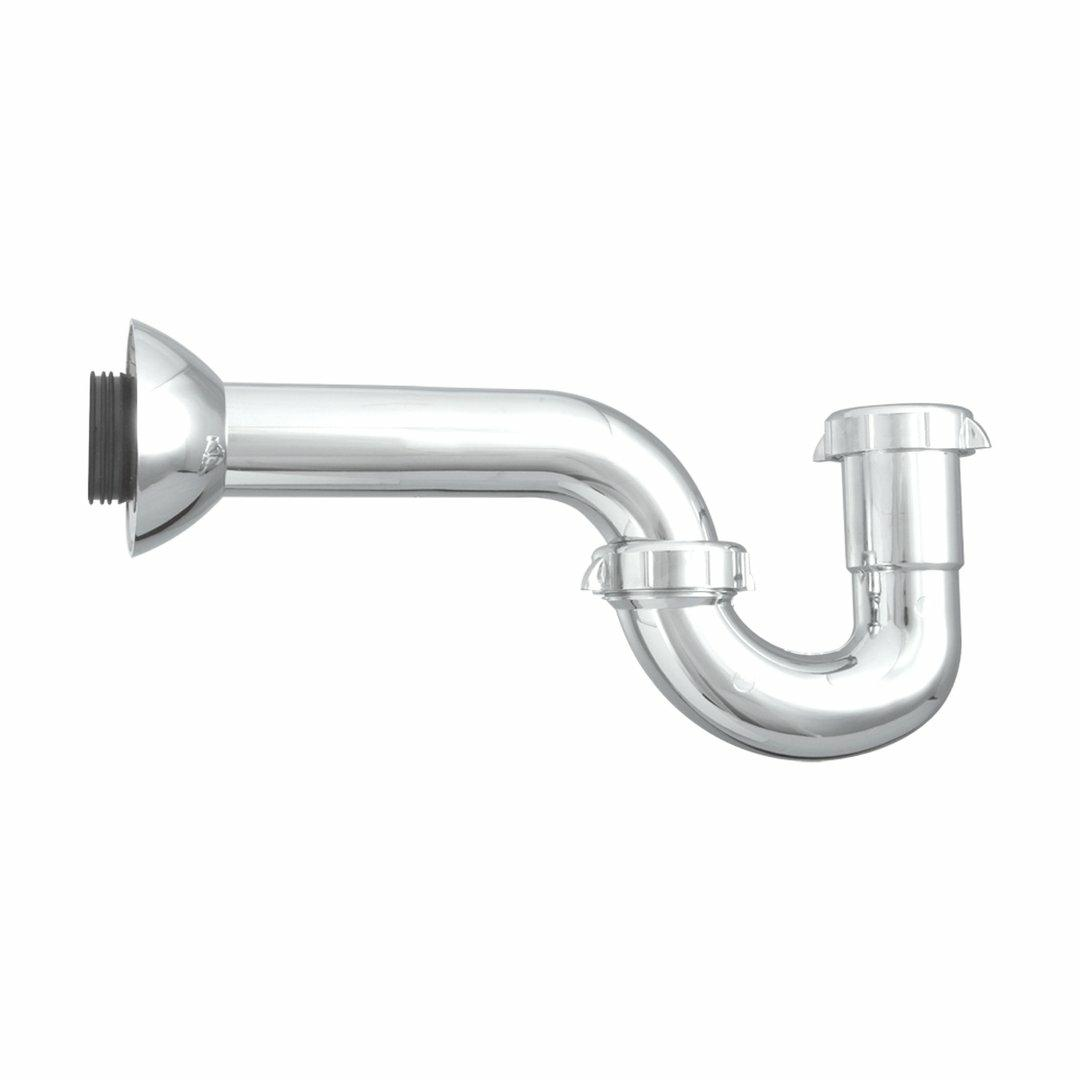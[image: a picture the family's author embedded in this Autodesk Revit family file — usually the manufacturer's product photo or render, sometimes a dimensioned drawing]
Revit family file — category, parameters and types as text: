
# Revit family: BIM_L1-3079-11
name_source: partatom
category: Aparatos sanitarios
units: mm (PartAtom-declared; Revit-internal decimal feet)

## family parameters
Activar corte en vistas = No
Anfitrión = Cara
Compartido = No
Corte con vacíos al cargar = No
Cota de conector redondo = Usar diámetro
Mantener orientación de anotación = No
Número OmniClass = 23.31.11.00
Punto de cálculo de habitación = No
Tipo de pieza = Normal

## types (1)
- L1-3079-11
    Acabado = Cepillado Brillante
    Alto = 190 mm
    Ancho = 1200 mm  [stored 3.93701 ft]
    Conexión AC = Sí
    Conexión AF = Sí
    Conexión de residuos = No
    Conexión de ventilación = No
    Date Modified = 08-08-2025
    Descripción = Lavaplatos en acero
    Elevación por defecto = 0 mm  [stored 0 ft]
    Fabricante = Gricol
    Garantia Especifica = 5 años
    Imagen de tipo = <Ninguno>
    Largo = 510 mm  [stored 1.67323 ft]
    Link Ficha Tecnica = https://infotecnica.gricol.com
    Material = Acero inoxidable
    Modelo = L1-3079-11
    Nota clave = INstalacion de grifería con unica perforación
    Peso = 4.00 kg
    Product Name = Lavaplatos Poceta Derecha 120 X 50 Cm Con Complementos
    Tipo de Uso = Si
    URL = https://www.gricol.com

note: [stored X ft] marks values corroborated as IEEE doubles in the binary element streams (Revit-internal decimal feet)

## geometry (parser evidence)
native form markers: Blend x2, Sweep x13
no freeform markers — native parametric forms only
